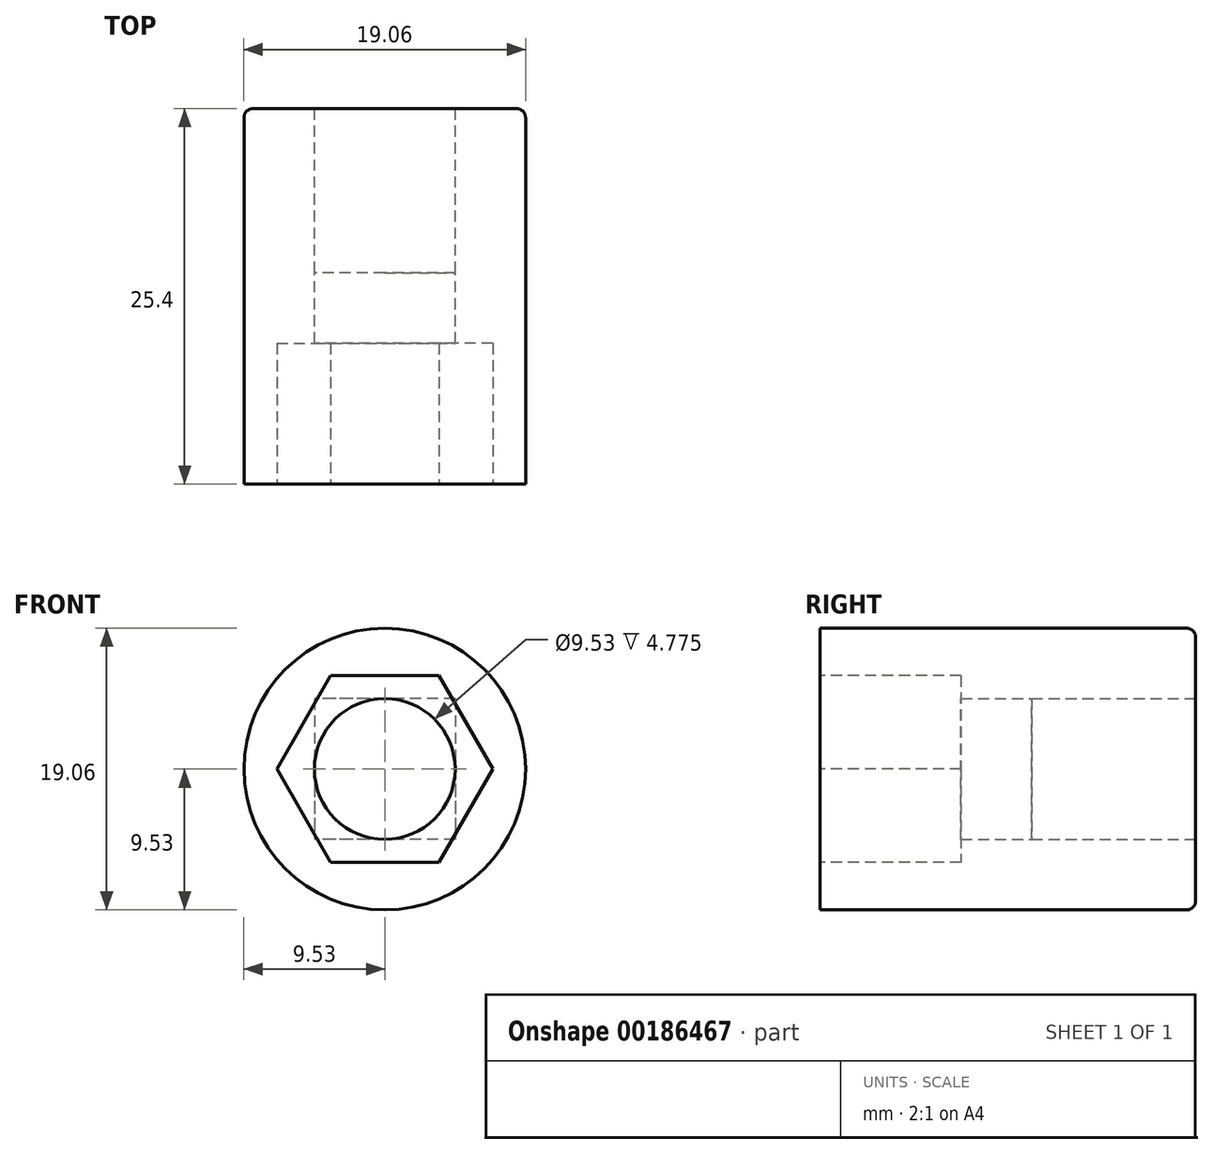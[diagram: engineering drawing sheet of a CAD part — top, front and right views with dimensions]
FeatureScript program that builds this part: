
annotation { "Feature Type Name" : "Feature", "Feature Type Description" : "" }
export const myFeature = defineFeature(function(context is Context, id is Id, definition is map)
    precondition{}
    {
        {
            var Q0;
            Q0=qCreatedBy(makeId("Front.planeOp"),FACE);
            var sketch = newSketch(context, id + "F0", { "sketchPlane" : qUnion([Q0])});
            skCircle(sketch, "E0", {"center": v(0, 0) * mm, "radius": 9.53 * mm});
            skSolve(sketch);
        }
        {
            var Q0;
            Q0=makeQuery(id+"F0.imprint","IMPRINT",FACE,{"disambiguationData":[TD([[makeQuery(id+"F0.imprint","IMPRINT",EDGE,{"derivedFrom":sQuery(id+"F0.wireOp",EDGE,"E0")}),1.0]])]});
            extrude(context, id + "F1", {"entities" : qUnion([Q0]), "depth" : 25.4 * mm});
        }
        {
            var Q0;
            Q0=qCreatedBy(makeId("Front.planeOp"),FACE);
            var sketch = newSketch(context, id + "F2", { "sketchPlane" : qUnion([Q0])});
            skLineSegment(sketch, "E1.bottom", {"start": v(4.76, 4.76) * mm, "end": v(-4.76, 4.76) * mm});
            skLineSegment(sketch, "E1.top", {"start": v(4.76, -4.76) * mm, "end": v(-4.76, -4.76) * mm});
            skLineSegment(sketch, "E1.left", {"start": v(4.76, 4.76) * mm, "end": v(4.76, -4.76) * mm});
            skLineSegment(sketch, "E1.right", {"start": v(-4.76, 4.76) * mm, "end": v(-4.76, -4.76) * mm});
            skPoint(sketch, "E1.middle", {"position": v(0, 0) * mm});
            skCircle(sketch, "E2", {"center": v(0, 0) * mm, "radius": 4.76 * mm});
            skSolve(sketch);
        }
        {
            var Q0;
            {var subQ0=sQuery(id+"F2.wireOp",EDGE,"E2");var subQ1=makeQuery(id+"F2.imprint","INTERSECT",VERTEX,{"derivedFrom":[sQuery(id+"F2.wireOp",EDGE,"E1.bottom"),subQ0]});Q0=makeQuery(id+"F2.imprint","IMPRINT",FACE,{"disambiguationData":[TD([[makeQuery(id+"F2.imprint","IMPRINT",EDGE,{"disambiguationData":[TD([[subQ1,1.0]])],"derivedFrom":subQ0}),1.0]])]});}
            extrude(context, id + "F3", {"entities" : qUnion([Q0]), "operationType" : NewBodyOperationType.REMOVE, "endBound" : BoundingType.THROUGH_ALL, "depth" : 25.4 * mm});
        }
        {
            var Q0;
            {var subQ0=sQuery(id+"F2.wireOp",EDGE,"E1.right");var subQ1=sQuery(id+"F2.wireOp",EDGE,"E1.top");var subQ2=makeQuery(id+"F2.imprint","INTERSECT",VERTEX,{"derivedFrom":[subQ1,subQ0]});Q0=makeQuery(id+"F2.imprint","IMPRINT",FACE,{"disambiguationData":[TD([[makeQuery(id+"F2.imprint","IMPRINT",EDGE,{"disambiguationData":[TD([[subQ2,1.0]])],"derivedFrom":subQ1}),-1.0]])]});}
            var Q1;
            {var subQ0=sQuery(id+"F2.wireOp",EDGE,"E1.right");var subQ1=sQuery(id+"F2.wireOp",EDGE,"E1.bottom");var subQ2=makeQuery(id+"F2.imprint","INTERSECT",VERTEX,{"derivedFrom":[subQ1,subQ0]});Q1=makeQuery(id+"F2.imprint","IMPRINT",FACE,{"disambiguationData":[TD([[makeQuery(id+"F2.imprint","IMPRINT",EDGE,{"disambiguationData":[TD([[subQ2,1.0]])],"derivedFrom":subQ1}),1.0]])]});}
            var Q2;
            {var subQ0=sQuery(id+"F2.wireOp",EDGE,"E1.left");var subQ1=sQuery(id+"F2.wireOp",EDGE,"E1.bottom");var subQ2=makeQuery(id+"F2.imprint","INTERSECT",VERTEX,{"derivedFrom":[subQ1,subQ0]});Q2=makeQuery(id+"F2.imprint","IMPRINT",FACE,{"disambiguationData":[TD([[makeQuery(id+"F2.imprint","IMPRINT",EDGE,{"disambiguationData":[TD([[subQ2,-1.0]])],"derivedFrom":subQ1}),1.0]])]});}
            var Q3;
            {var subQ0=sQuery(id+"F2.wireOp",EDGE,"E1.left");var subQ1=sQuery(id+"F2.wireOp",EDGE,"E1.top");var subQ2=makeQuery(id+"F2.imprint","INTERSECT",VERTEX,{"derivedFrom":[subQ1,subQ0]});Q3=makeQuery(id+"F2.imprint","IMPRINT",FACE,{"disambiguationData":[TD([[makeQuery(id+"F2.imprint","IMPRINT",EDGE,{"disambiguationData":[TD([[subQ2,-1.0]])],"derivedFrom":subQ1}),-1.0]])]});}
            extrude(context, id + "F4", {"entities" : qUnion([Q0, Q1, Q2, Q3]), "operationType" : NewBodyOperationType.REMOVE, "depth" : 11.1 * mm});
        }
        {
            var Q0;
            Q0=makeQuery(id+"F1.opExtrude","CAP_FACE",FACE,{"disambiguationData":[OSD([sQuery(id+"F0.wireOp",EDGE,"E0")])],"isStart":false});
            var sketch = newSketch(context, id + "F5", { "sketchPlane" : qUnion([Q0])});
            skCircle(sketch, "E3.cCircle", {"center": v(0, 0) * mm, "radius": 7.3 * mm, "construction": true});
            skLineSegment(sketch, "E3.0", {"start": v(7.3, 0) * mm, "end": v(3.65, -6.32) * mm});
            skLineSegment(sketch, "E3.1", {"start": v(3.65, -6.32) * mm, "end": v(-3.65, -6.32) * mm});
            skLineSegment(sketch, "E3.2", {"start": v(-3.65, -6.32) * mm, "end": v(-7.3, 0) * mm});
            skLineSegment(sketch, "E3.3", {"start": v(-7.3, 0) * mm, "end": v(-3.65, 6.32) * mm});
            skLineSegment(sketch, "E3.4", {"start": v(-3.65, 6.32) * mm, "end": v(3.65, 6.32) * mm});
            skLineSegment(sketch, "E3.5", {"start": v(3.65, 6.32) * mm, "end": v(7.3, 0) * mm});
            skSolve(sketch);
        }
        {
            var Q0;
            Q0 = qSketchRegion(id + "F5", true);
            extrude(context, id + "F6", {"entities" : qUnion([Q0]), "operationType" : NewBodyOperationType.REMOVE, "oppositeDirection" : true, "depth" : 9.52 * mm});
        }
        {
            var Q0;
            Q0=makeQuery(id+"F1.opExtrude","CAP_EDGE",EDGE,{"disambiguationData":[OSD([sQuery(id+"F0.wireOp",EDGE,"E0")])],"isStart":true});
            fillet(context, id + "F7", {"entities" : qUnion([Q0]), "radius" : 0.61 * mm, "tangentPropagation" : true, "allowEdgeOverflow" : false});
        }
    });
